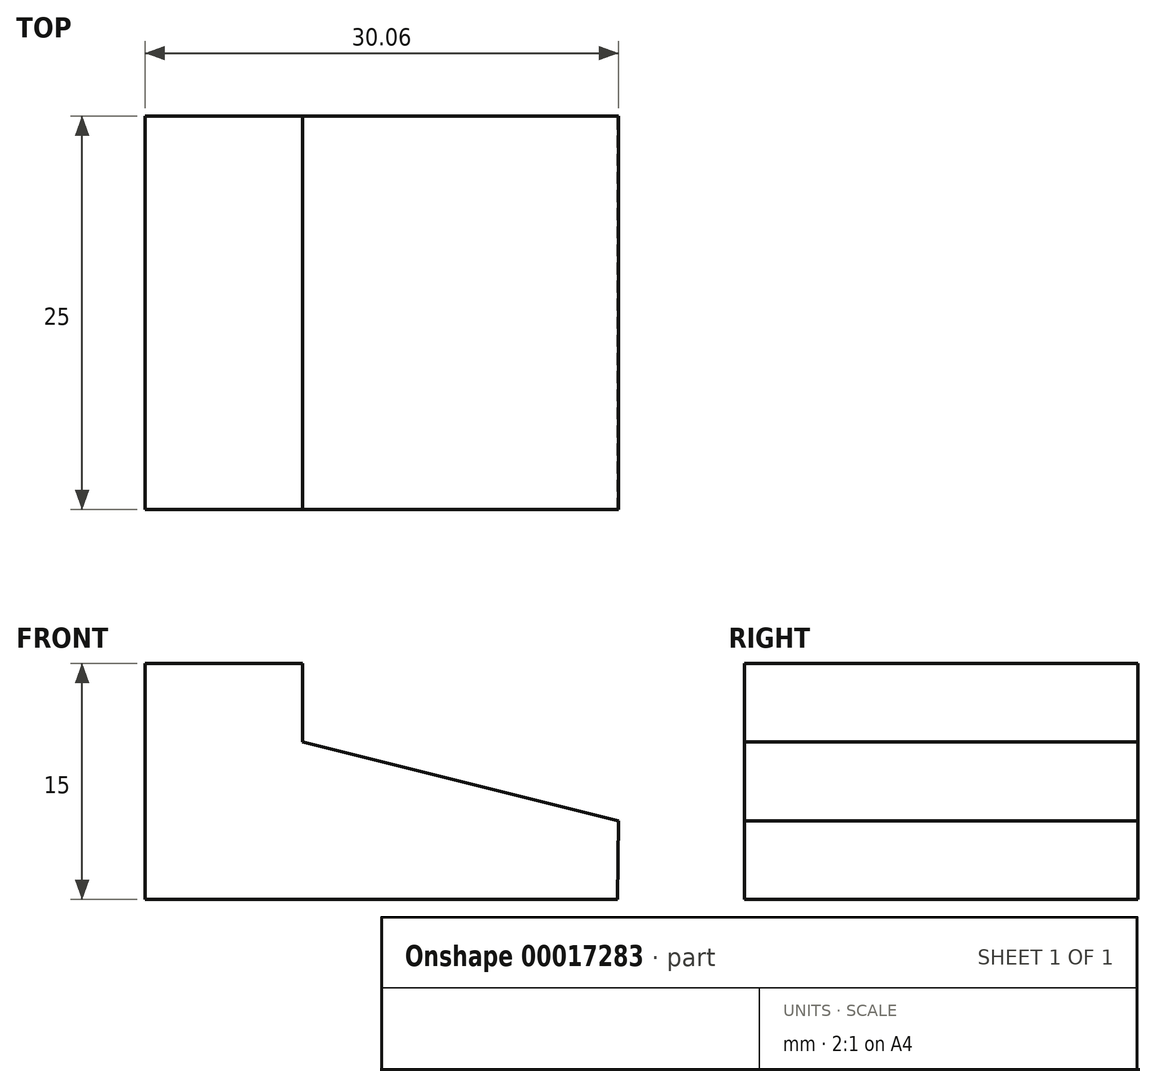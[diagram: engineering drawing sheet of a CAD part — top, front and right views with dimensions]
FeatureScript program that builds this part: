
annotation { "Feature Type Name" : "Feature", "Feature Type Description" : "" }
export const myFeature = defineFeature(function(context is Context, id is Id, definition is map)
    precondition{}
    {
        {
            var Q0;
            Q0=qCreatedBy(makeId("Front.planeOp"),FACE);
            var sketch = newSketch(context, id + "F0", { "sketchPlane" : qUnion([Q0])});
            skLineSegment(sketch, "E0", {"start": v(-24.01, 15) * mm, "end": v(-24.01, 0) * mm});
            skLineSegment(sketch, "E1", {"start": v(-24.01, 0) * mm, "end": v(5.99, 0) * mm});
            skLineSegment(sketch, "E2", {"start": v(5.99, 0) * mm, "end": v(6.05, 5) * mm});
            skLineSegment(sketch, "E3", {"start": v(6.05, 5) * mm, "end": v(-14.01, 10) * mm});
            skLineSegment(sketch, "E4", {"start": v(-14.01, 15) * mm, "end": v(-14.01, 10) * mm});
            skLineSegment(sketch, "E5", {"start": v(-14.01, 15) * mm, "end": v(-24.01, 15) * mm});
            skSolve(sketch);
        }
        {
            var Q0;
            Q0=makeQuery(id+"F0.imprint","IMPRINT",FACE,{"disambiguationData":[TD([[makeQuery(id+"F0.imprint","IMPRINT",EDGE,{"derivedFrom":sQuery(id+"F0.wireOp",EDGE,"E0")}),1.0]])]});
            extrude(context, id + "F1", {"entities" : qUnion([Q0]), "depth" : 25 * mm});
        }
    });
